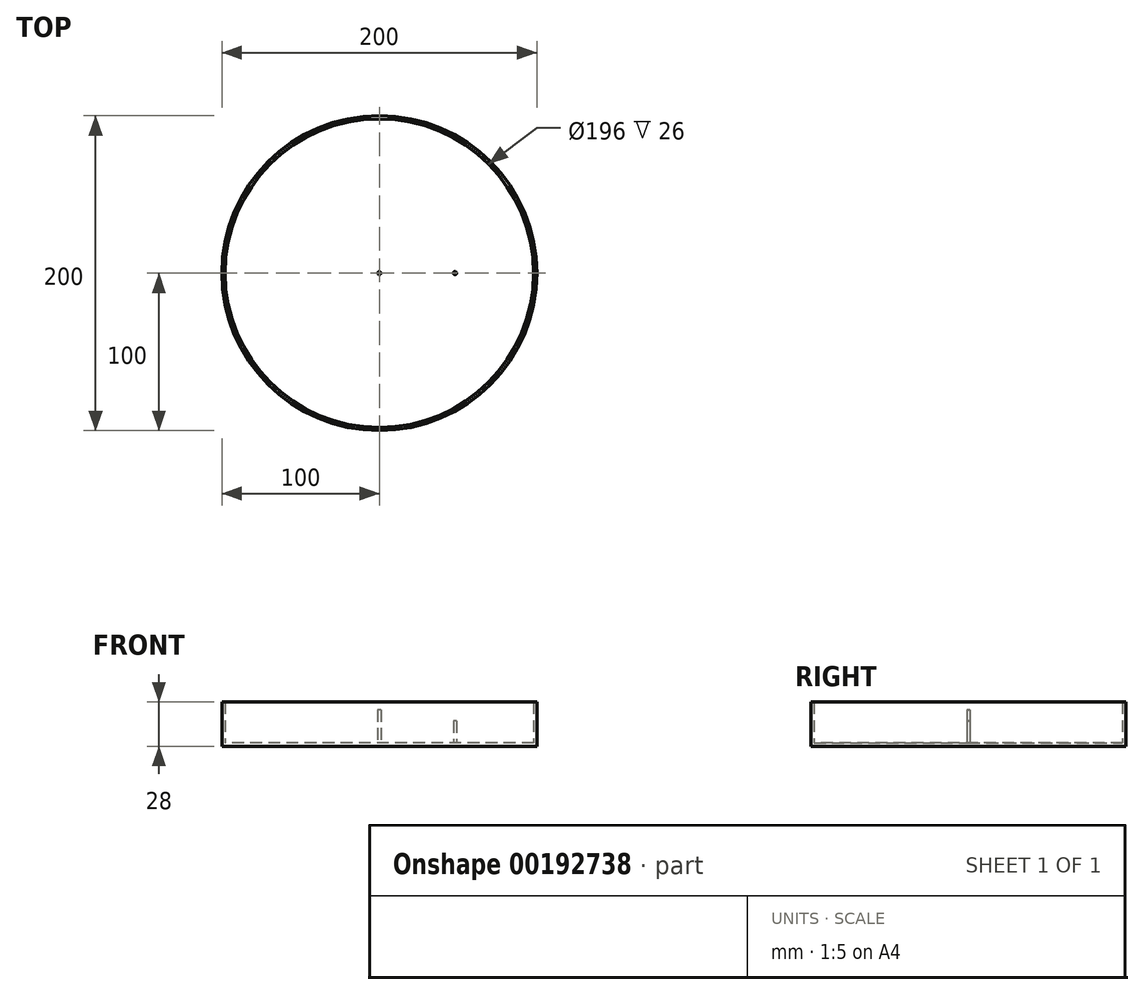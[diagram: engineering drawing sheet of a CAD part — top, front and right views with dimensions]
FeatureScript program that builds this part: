
annotation { "Feature Type Name" : "Feature", "Feature Type Description" : "" }
export const myFeature = defineFeature(function(context is Context, id is Id, definition is map)
    precondition{}
    {
        {
            var Q0;
            Q0=qCreatedBy(makeId("Top.planeOp"),FACE);
            var sketch = newSketch(context, id + "F0", { "sketchPlane" : qUnion([Q0])});
            skCircle(sketch, "E0", {"center": v(0, 0) * mm, "radius": 100 * mm});
            skSolve(sketch);
        }
        {
            var Q0;
            Q0 = qSketchRegion(id + "F0", true);
            extrude(context, id + "F1", {"entities" : qUnion([Q0]), "depth" : 28 * mm});
        }
        {
            var Q0;
            Q0=makeQuery(id+"F1.opExtrude","CAP_FACE",FACE,{"disambiguationData":[OSD([sQuery(id+"F0.wireOp",EDGE,"E0")])],"isStart":false});
            shell(context, id + "F2", {"entities" : qUnion([Q0]), "thickness" : 2 * mm});
        }
        {
            var Q0;
            {var subQ0=sQuery(id+"F0.wireOp",EDGE,"E0");Q0=makeQuery(id+"F2.opShell","OFFSET_FACE",FACE,{"disambiguationData":[OSD([subQ0]),TDD([makeQuery(id+"F1.opExtrude","CAP_FACE",FACE,{"disambiguationData":[OSD([subQ0])],"isStart":true})])]});}
            var sketch = newSketch(context, id + "F3", { "sketchPlane" : qUnion([Q0])});
            skCircle(sketch, "E1", {"center": v(0, 0) * mm, "radius": 1 * mm});
            skSolve(sketch);
        }
        {
            var Q0;
            Q0 = qSketchRegion(id + "F3", true);
            extrude(context, id + "F4", {"entities" : qUnion([Q0]), "operationType" : NewBodyOperationType.ADD, "depth" : 21 * mm});
        }
        {
            var Q0;
            {var subQ0=sQuery(id+"F0.wireOp",EDGE,"E0");Q0=makeQuery(id+"F2.opShell","OFFSET_FACE",FACE,{"disambiguationData":[OSD([subQ0]),TDD([makeQuery(id+"F1.opExtrude","CAP_FACE",FACE,{"disambiguationData":[OSD([subQ0])],"isStart":true})])]});}
            var sketch = newSketch(context, id + "F5", { "sketchPlane" : qUnion([Q0])});
            skCircle(sketch, "E2", {"center": v(48, 0) * mm, "radius": 1 * mm});
            skSolve(sketch);
        }
        {
            var Q0;
            Q0 = qSketchRegion(id + "F5", true);
            extrude(context, id + "F6", {"entities" : qUnion([Q0]), "operationType" : NewBodyOperationType.ADD, "depth" : 14 * mm});
        }
    });
